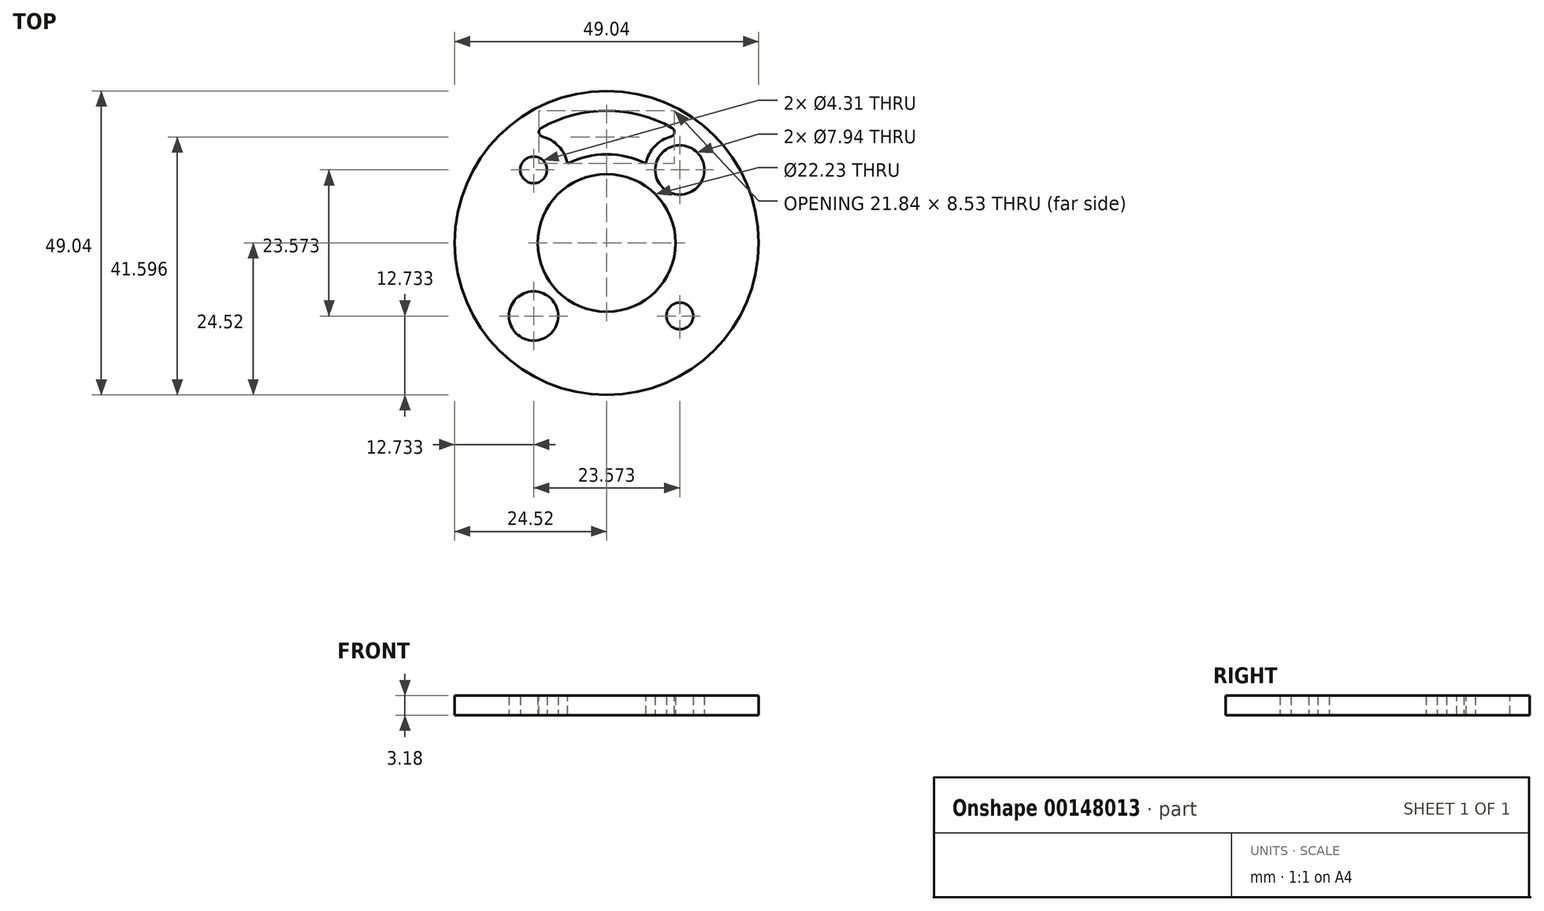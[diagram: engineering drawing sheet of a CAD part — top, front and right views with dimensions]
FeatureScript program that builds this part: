
annotation { "Feature Type Name" : "Feature", "Feature Type Description" : "" }
export const myFeature = defineFeature(function(context is Context, id is Id, definition is map)
    precondition{}
    {
        {
            var Q0;
            Q0=qCreatedBy(makeId("Top.planeOp"),FACE);
            var sketch = newSketch(context, id + "F0", { "sketchPlane" : qUnion([Q0])});
            skCircle(sketch, "E0", {"center": v(0, 0) * mm, "radius": 24.52 * mm});
            skCircle(sketch, "E1", {"center": v(0, 0) * mm, "radius": 11.11 * mm});
            skLineSegment(sketch, "E2.bottom", {"start": v(-11.79, 11.79) * mm, "end": v(11.79, 11.79) * mm, "construction": true});
            skLineSegment(sketch, "E2.top", {"start": v(-11.79, -11.79) * mm, "end": v(11.79, -11.79) * mm, "construction": true});
            skLineSegment(sketch, "E2.left", {"start": v(-11.79, 11.79) * mm, "end": v(-11.79, -11.79) * mm, "construction": true});
            skLineSegment(sketch, "E2.right", {"start": v(11.79, 11.79) * mm, "end": v(11.79, -11.79) * mm, "construction": true});
            skCircle(sketch, "E3", {"center": v(-11.79, 11.79) * mm, "radius": 5.56 * mm, "construction": true});
            skCircle(sketch, "E4", {"center": v(11.79, 11.79) * mm, "radius": 2.15 * mm, "construction": true});
            skCircle(sketch, "E5", {"center": v(-11.79, 11.79) * mm, "radius": 2.15 * mm});
            skCircle(sketch, "E6", {"center": v(-11.79, -11.79) * mm, "radius": 2.15 * mm, "construction": true});
            skCircle(sketch, "E7", {"center": v(11.79, -11.79) * mm, "radius": 2.15 * mm});
            skCircle(sketch, "E8", {"center": v(-11.79, -11.79) * mm, "radius": 3.97 * mm});
            skCircle(sketch, "E9", {"center": v(11.79, 11.79) * mm, "radius": 3.97 * mm});
            skSolve(sketch);
        }
        {
            var Q0;
            Q0=qSketchRegion(id+"F0",true);
            extrude(context, id + "F1", {"entities" : qUnion([Q0]), "depth" : 3.17 * mm});
        }
        {
            var Q0;
            Q0=makeQuery(id+"F1.opExtrude","CAP_FACE",FACE,{"disambiguationData":[OSD([sQuery(id+"F0.wireOp",EDGE,"E0"),sQuery(id+"F0.wireOp",EDGE,"E1"),sQuery(id+"F0.wireOp",EDGE,"E4"),sQuery(id+"F0.wireOp",EDGE,"E5"),sQuery(id+"F0.wireOp",EDGE,"E6"),sQuery(id+"F0.wireOp",EDGE,"E7")])],"isStart":false});
            var sketch = newSketch(context, id + "F2", { "sketchPlane" : qUnion([Q0])});
            skArc(sketch, "E10", {"start": v(-6.33, 12.81) * mm, "mid": v(-8.52, 16.28) * mm, "end": v(-12.5, 17.3) * mm});
            skArc(sketch, "E11", {"start": v(12.5, 17.3) * mm, "mid": v(8.52, 16.28) * mm, "end": v(6.33, 12.81) * mm});
            skArc(sketch, "E12", {"start": v(12.5, 17.3) * mm, "mid": v(0, 21.34) * mm, "end": v(-12.5, 17.3) * mm});
            skArc(sketch, "E13", {"start": v(6.33, 12.81) * mm, "mid": v(0, 14.29) * mm, "end": v(-6.33, 12.81) * mm});
            skSolve(sketch);
        }
        {
            var Q0;
            Q0=makeQuery(id+"F2.imprint","IMPRINT",FACE,{"disambiguationData":[TD([[makeQuery(id+"F2.imprint","IMPRINT",EDGE,{"derivedFrom":sQuery(id+"F2.wireOp",EDGE,"E10")}),-1.0]])]});
            var Q1;
            Q1=makeQuery(id+"F1.opExtrude","CAP_FACE",FACE,{"disambiguationData":[OSD([sQuery(id+"F0.wireOp",EDGE,"E0"),sQuery(id+"F0.wireOp",EDGE,"E1"),sQuery(id+"F0.wireOp",EDGE,"E4"),sQuery(id+"F0.wireOp",EDGE,"E5"),sQuery(id+"F0.wireOp",EDGE,"E6"),sQuery(id+"F0.wireOp",EDGE,"E7")])],"isStart":true});
            extrude(context, id + "F3", {"entities" : qUnion([Q0]), "operationType" : NewBodyOperationType.REMOVE, "endBound" : BoundingType.UP_TO_SURFACE, "oppositeDirection" : true, "endBoundEntityFace" : qUnion([Q1]), "depth" : 25.4 * mm});
        }
        {
            var Q0;
            Q0=makeQuery(id+"F6MqURjXbY15YYN_1.1.F3.boolean.opBoolean","COPY",EDGE,{"derivedFrom":makeQuery(id+"F6MqURjXbY15YYN_1.1.F3.opExtrude","SWEPT_EDGE",EDGE,{"disambiguationData":[OSD([sQuery(id+"F2.wireOp",EDGE,"E10"),sQuery(id+"F2.wireOp",EDGE,"E12")])]})});
            var Q1;
            Q1=makeQuery(id+"F6MqURjXbY15YYN_1.1.F3.boolean.opBoolean","COPY",EDGE,{"derivedFrom":makeQuery(id+"F6MqURjXbY15YYN_1.1.F3.opExtrude","SWEPT_EDGE",EDGE,{"disambiguationData":[OSD([sQuery(id+"F2.wireOp",EDGE,"E11"),sQuery(id+"F2.wireOp",EDGE,"E12")])]})});
            var Q2;
            Q2=makeQuery(id+"F6MqURjXbY15YYN_1.2.F3.boolean.opBoolean","COPY",EDGE,{"derivedFrom":makeQuery(id+"F6MqURjXbY15YYN_1.2.F3.opExtrude","SWEPT_EDGE",EDGE,{"disambiguationData":[OSD([sQuery(id+"F2.wireOp",EDGE,"E10"),sQuery(id+"F2.wireOp",EDGE,"E12")])]})});
            var Q3;
            Q3=makeQuery(id+"F6MqURjXbY15YYN_1.2.F3.boolean.opBoolean","COPY",EDGE,{"derivedFrom":makeQuery(id+"F6MqURjXbY15YYN_1.2.F3.opExtrude","SWEPT_EDGE",EDGE,{"disambiguationData":[OSD([sQuery(id+"F2.wireOp",EDGE,"E11"),sQuery(id+"F2.wireOp",EDGE,"E12")])]})});
            var Q4;
            Q4=makeQuery(id+"F6MqURjXbY15YYN_1.3.F3.boolean.opBoolean","COPY",EDGE,{"derivedFrom":makeQuery(id+"F6MqURjXbY15YYN_1.3.F3.opExtrude","SWEPT_EDGE",EDGE,{"disambiguationData":[OSD([sQuery(id+"F2.wireOp",EDGE,"E10"),sQuery(id+"F2.wireOp",EDGE,"E12")])]})});
            var Q5;
            Q5=makeQuery(id+"F6MqURjXbY15YYN_1.3.F3.boolean.opBoolean","COPY",EDGE,{"derivedFrom":makeQuery(id+"F6MqURjXbY15YYN_1.3.F3.opExtrude","SWEPT_EDGE",EDGE,{"disambiguationData":[OSD([sQuery(id+"F2.wireOp",EDGE,"E11"),sQuery(id+"F2.wireOp",EDGE,"E12")])]})});
            var Q6;
            Q6=makeQuery(id+"F3.boolean.opBoolean","COPY",EDGE,{"derivedFrom":makeQuery(id+"F3.opExtrude","SWEPT_EDGE",EDGE,{"disambiguationData":[OSD([sQuery(id+"F2.wireOp",EDGE,"E10"),sQuery(id+"F2.wireOp",EDGE,"E12")])]})});
            var Q7;
            Q7=makeQuery(id+"F3.boolean.opBoolean","COPY",EDGE,{"derivedFrom":makeQuery(id+"F3.opExtrude","SWEPT_EDGE",EDGE,{"disambiguationData":[OSD([sQuery(id+"F2.wireOp",EDGE,"E11"),sQuery(id+"F2.wireOp",EDGE,"E12")])]})});
            fillet(context, id + "F4", {"entities" : qUnion([Q0, Q1, Q2, Q3, Q4, Q5, Q6, Q7]), "radius" : 0.76 * mm, "tangentPropagation" : true, "allowEdgeOverflow" : false});
        }
    });
